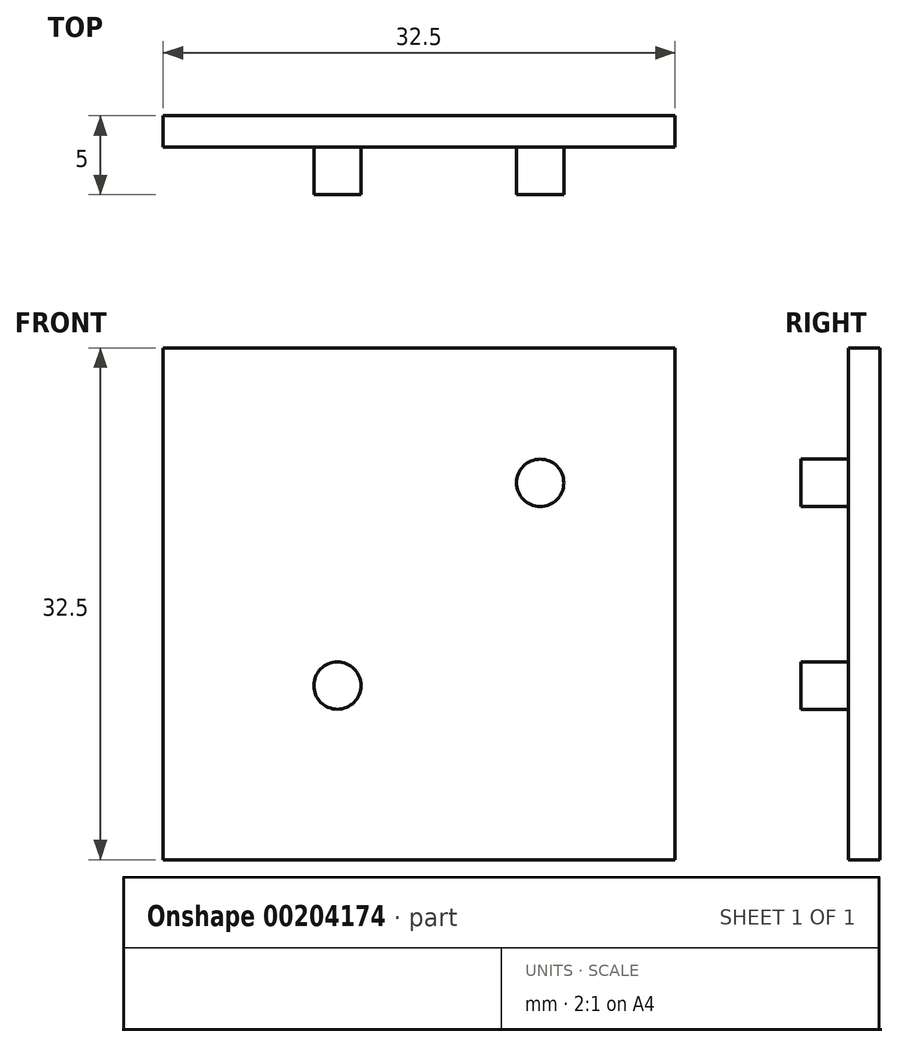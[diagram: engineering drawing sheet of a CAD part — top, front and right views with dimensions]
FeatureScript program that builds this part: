
annotation { "Feature Type Name" : "Feature", "Feature Type Description" : "" }
export const myFeature = defineFeature(function(context is Context, id is Id, definition is map)
    precondition{}
    {
        {
            var Q0;
            Q0=qCreatedBy(makeId("Top.planeOp"),FACE);
            var sketch = newSketch(context, id + "F0", { "sketchPlane" : qUnion([Q0])});
            skLineSegment(sketch, "E0.bottom", {"start": v(-16.25, 1) * mm, "end": v(16.25, 1) * mm});
            skLineSegment(sketch, "E0.top", {"start": v(-16.25, -1) * mm, "end": v(16.25, -1) * mm});
            skLineSegment(sketch, "E0.left", {"start": v(-16.25, 1) * mm, "end": v(-16.25, -1) * mm});
            skLineSegment(sketch, "E0.right", {"start": v(16.25, 1) * mm, "end": v(16.25, -1) * mm});
            skPoint(sketch, "E0.middle", {"position": v(0, 0) * mm});
            skSolve(sketch);
        }
        {
            var Q0;
            Q0 = qSketchRegion(id + "F0", true);
            extrude(context, id + "F1", {"entities" : qUnion([Q0]), "depth" : 32.5 * mm});
        }
        {
            var Q0;
            Q0=makeQuery(id+"F1.opExtrude","SWEPT_FACE",FACE,{"disambiguationData":[OSD([sQuery(id+"F0.wireOp",EDGE,"E0.top")])]});
            var sketch = newSketch(context, id + "F2", { "sketchPlane" : qUnion([Q0])});
            skLineSegment(sketch, "E1.bottom", {"start": v(16.25, 32.5) * mm, "end": v(8.75, 32.5) * mm, "construction": true});
            skLineSegment(sketch, "E1.top", {"start": v(16.25, 25) * mm, "end": v(8.75, 25) * mm, "construction": true});
            skLineSegment(sketch, "E1.left", {"start": v(16.25, 32.5) * mm, "end": v(16.25, 25) * mm, "construction": true});
            skLineSegment(sketch, "E1.right", {"start": v(8.75, 32.5) * mm, "end": v(8.75, 25) * mm, "construction": true});
            skLineSegment(sketch, "E2.bottom", {"start": v(8.75, 25) * mm, "end": v(-6.25, 25) * mm, "construction": true});
            skLineSegment(sketch, "E2.top", {"start": v(8.75, 10) * mm, "end": v(-6.25, 10) * mm, "construction": true});
            skLineSegment(sketch, "E2.left", {"start": v(8.75, 25) * mm, "end": v(8.75, 10) * mm, "construction": true});
            skLineSegment(sketch, "E2.right", {"start": v(-6.25, 25) * mm, "end": v(-6.25, 10) * mm, "construction": true});
            skLineSegment(sketch, "E3", {"start": v(-6.25, 10) * mm, "end": v(-5.19, 11.06) * mm, "construction": true});
            skLineSegment(sketch, "E4", {"start": v(-5.19, 11.06) * mm, "end": v(7.69, 23.94) * mm, "construction": true});
            skLineSegment(sketch, "E5", {"start": v(7.69, 23.94) * mm, "end": v(8.75, 25) * mm, "construction": true});
            skCircle(sketch, "E6", {"center": v(-5.19, 11.06) * mm, "radius": 1.5 * mm});
            skCircle(sketch, "E7", {"center": v(7.69, 23.94) * mm, "radius": 1.5 * mm});
            skSolve(sketch);
        }
        {
            var Q0;
            Q0 = qSketchRegion(id + "F2", true);
            extrude(context, id + "F3", {"entities" : qUnion([Q0]), "operationType" : NewBodyOperationType.ADD, "depth" : 3 * mm});
        }
    });
